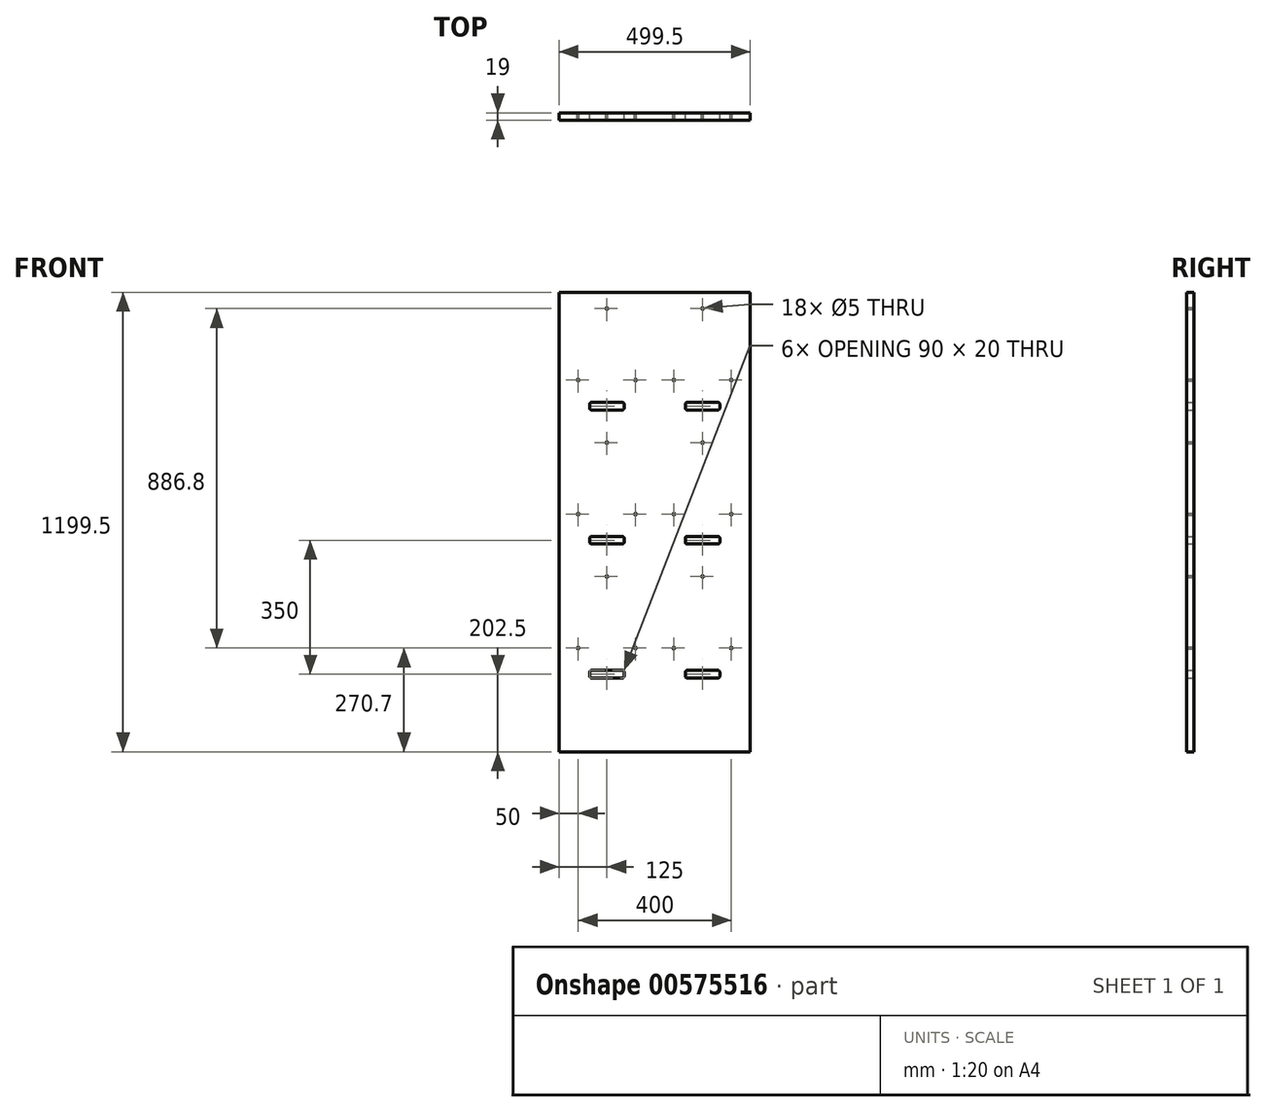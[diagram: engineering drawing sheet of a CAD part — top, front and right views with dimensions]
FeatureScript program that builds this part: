
annotation { "Feature Type Name" : "Feature", "Feature Type Description" : "" }
export const myFeature = defineFeature(function(context is Context, id is Id, definition is map)
    precondition{}
    {
        {
            var Q0;
            Q0=qCreatedBy(makeId("Front.planeOp"),FACE);
            var sketch = newSketch(context, id + "F0", { "sketchPlane" : qUnion([Q0])});
            skLineSegment(sketch, "E0.bottom", {"start": v(0, 0) * mm, "end": v(1000, 0) * mm, "construction": true});
            skLineSegment(sketch, "E0.left", {"start": v(0, 0) * mm, "end": v(0, 1590) * mm, "construction": true});
            skLineSegment(sketch, "E0.right", {"start": v(1000, 0) * mm, "end": v(1000, 1590) * mm, "construction": true});
            skLineSegment(sketch, "E1", {"start": v(500, 1590) * mm, "end": v(500, 0) * mm, "construction": true});
            skLineSegment(sketch, "E2.bottom", {"start": v(0, 1590) * mm, "end": v(1000, 1590) * mm, "construction": true});
            skLineSegment(sketch, "E2.left", {"start": v(0, 1590) * mm, "end": v(0, 290) * mm, "construction": true});
            skSolve(sketch);
        }
        {
            var Q0;
            Q0=qCreatedBy(makeId("Front.planeOp"),FACE);
            var sketch = newSketch(context, id + "F1", { "sketchPlane" : qUnion([Q0])});
            skLineSegment(sketch, "E3.bottom", {"start": v(0, 1590) * mm, "end": v(499.5, 1590) * mm});
            skLineSegment(sketch, "E3.top", {"start": v(0, 390.5) * mm, "end": v(499.5, 390.5) * mm});
            skLineSegment(sketch, "E3.left", {"start": v(0, 1590) * mm, "end": v(0, 390.5) * mm});
            skLineSegment(sketch, "E3.right", {"start": v(499.5, 1590) * mm, "end": v(499.5, 390.5) * mm});
            skLineSegment(sketch, "E4", {"start": v(125, 1590) * mm, "end": v(125, 390.5) * mm, "construction": true});
            skLineSegment(sketch, "E5", {"start": v(375, 1590) * mm, "end": v(375, 390.5) * mm, "construction": true});
            skCircle(sketch, "E6", {"center": v(125, 1548) * mm, "radius": 2.5 * mm});
            skCircle(sketch, "E7", {"center": v(50, 1361.2) * mm, "radius": 2.5 * mm});
            skCircle(sketch, "E8.MirrorC", {"center": v(200, 1361.2) * mm, "radius": 2.5 * mm});
            skLineSegment(sketch, "E9.bottom", {"start": v(165, 1283) * mm, "end": v(85, 1283) * mm});
            skLineSegment(sketch, "E9.top", {"start": v(165, 1303) * mm, "end": v(85, 1303) * mm});
            skLineSegment(sketch, "E9.left", {"start": v(170, 1288) * mm, "end": v(170, 1298) * mm});
            skLineSegment(sketch, "E9.right", {"start": v(80, 1288) * mm, "end": v(80, 1298) * mm});
            skPoint(sketch, "E9.middle", {"position": v(125, 1293) * mm});
            skPoint(sketch, "E10.visualSharp", {"position": v(80, 1303) * mm});
            skArc(sketch, "E10.filletArc", {"start": v(85, 1303) * mm, "mid": v(81.46, 1301.54) * mm, "end": v(80, 1298) * mm});
            skPoint(sketch, "E11.visualSharp", {"position": v(80, 1283) * mm});
            skArc(sketch, "E11.filletArc", {"start": v(80, 1288) * mm, "mid": v(81.46, 1284.46) * mm, "end": v(85, 1283) * mm});
            skPoint(sketch, "E12.visualSharp", {"position": v(170, 1283) * mm});
            skArc(sketch, "E12.filletArc", {"start": v(165, 1283) * mm, "mid": v(168.54, 1284.46) * mm, "end": v(170, 1288) * mm});
            skPoint(sketch, "E13.visualSharp", {"position": v(170, 1303) * mm});
            skArc(sketch, "E13.filletArc", {"start": v(170, 1298) * mm, "mid": v(168.54, 1301.54) * mm, "end": v(165, 1303) * mm});
            skLineSegment(sketch, "E14.0.1.0", {"start": v(165, 953) * mm, "end": v(85, 953) * mm});
            skPoint(sketch, "E14.0.1.1", {"position": v(125, 943) * mm});
            skPoint(sketch, "E14.0.1.2", {"position": v(80, 953) * mm});
            skPoint(sketch, "E14.0.1.3", {"position": v(80, 933) * mm});
            skPoint(sketch, "E14.0.1.4", {"position": v(170, 953) * mm});
            skLineSegment(sketch, "E14.0.1.5", {"start": v(165, 933) * mm, "end": v(85, 933) * mm});
            skPoint(sketch, "E14.0.1.6", {"position": v(170, 933) * mm});
            skCircle(sketch, "E14.0.1.7", {"center": v(125, 1198) * mm, "radius": 2.5 * mm});
            skCircle(sketch, "E14.0.1.8", {"center": v(200, 1011.2) * mm, "radius": 2.5 * mm});
            skCircle(sketch, "E14.0.1.9", {"center": v(50, 1011.2) * mm, "radius": 2.5 * mm});
            skArc(sketch, "E14.0.1.10", {"start": v(170, 948) * mm, "mid": v(168.54, 951.54) * mm, "end": v(165, 953) * mm});
            skArc(sketch, "E14.0.1.11", {"start": v(165, 933) * mm, "mid": v(168.54, 934.46) * mm, "end": v(170, 938) * mm});
            skArc(sketch, "E14.0.1.12", {"start": v(85, 953) * mm, "mid": v(81.46, 951.54) * mm, "end": v(80, 948) * mm});
            skLineSegment(sketch, "E14.0.1.13", {"start": v(170, 938) * mm, "end": v(170, 948) * mm});
            skLineSegment(sketch, "E14.0.1.14", {"start": v(80, 938) * mm, "end": v(80, 948) * mm});
            skArc(sketch, "E14.0.1.15", {"start": v(80, 938) * mm, "mid": v(81.46, 934.46) * mm, "end": v(85, 933) * mm});
            skLineSegment(sketch, "E14.0.2.0", {"start": v(165, 603) * mm, "end": v(85, 603) * mm});
            skPoint(sketch, "E14.0.2.1", {"position": v(125, 593) * mm});
            skPoint(sketch, "E14.0.2.2", {"position": v(80, 603) * mm});
            skPoint(sketch, "E14.0.2.3", {"position": v(80, 583) * mm});
            skPoint(sketch, "E14.0.2.4", {"position": v(170, 603) * mm});
            skLineSegment(sketch, "E14.0.2.5", {"start": v(165, 583) * mm, "end": v(85, 583) * mm});
            skPoint(sketch, "E14.0.2.6", {"position": v(170, 583) * mm});
            skCircle(sketch, "E14.0.2.7", {"center": v(125, 848) * mm, "radius": 2.5 * mm});
            skCircle(sketch, "E14.0.2.8", {"center": v(200, 661.2) * mm, "radius": 2.5 * mm});
            skCircle(sketch, "E14.0.2.9", {"center": v(50, 661.2) * mm, "radius": 2.5 * mm});
            skArc(sketch, "E14.0.2.10", {"start": v(170, 598) * mm, "mid": v(168.54, 601.54) * mm, "end": v(165, 603) * mm});
            skArc(sketch, "E14.0.2.11", {"start": v(165, 583) * mm, "mid": v(168.54, 584.46) * mm, "end": v(170, 588) * mm});
            skArc(sketch, "E14.0.2.12", {"start": v(85, 603) * mm, "mid": v(81.46, 601.54) * mm, "end": v(80, 598) * mm});
            skLineSegment(sketch, "E14.0.2.13", {"start": v(170, 588) * mm, "end": v(170, 598) * mm});
            skLineSegment(sketch, "E14.0.2.14", {"start": v(80, 588) * mm, "end": v(80, 598) * mm});
            skArc(sketch, "E14.0.2.15", {"start": v(80, 588) * mm, "mid": v(81.46, 584.46) * mm, "end": v(85, 583) * mm});
            skLineSegment(sketch, "E14.1.0.0", {"start": v(415, 1303) * mm, "end": v(335, 1303) * mm});
            skPoint(sketch, "E14.1.0.1", {"position": v(375, 1293) * mm});
            skPoint(sketch, "E14.1.0.2", {"position": v(330, 1303) * mm});
            skPoint(sketch, "E14.1.0.3", {"position": v(330, 1283) * mm});
            skPoint(sketch, "E14.1.0.4", {"position": v(420, 1303) * mm});
            skLineSegment(sketch, "E14.1.0.5", {"start": v(415, 1283) * mm, "end": v(335, 1283) * mm});
            skPoint(sketch, "E14.1.0.6", {"position": v(420, 1283) * mm});
            skCircle(sketch, "E14.1.0.7", {"center": v(375, 1548) * mm, "radius": 2.5 * mm});
            skCircle(sketch, "E14.1.0.8", {"center": v(450, 1361.2) * mm, "radius": 2.5 * mm});
            skCircle(sketch, "E14.1.0.9", {"center": v(300, 1361.2) * mm, "radius": 2.5 * mm});
            skArc(sketch, "E14.1.0.10", {"start": v(420, 1298) * mm, "mid": v(418.54, 1301.54) * mm, "end": v(415, 1303) * mm});
            skArc(sketch, "E14.1.0.11", {"start": v(415, 1283) * mm, "mid": v(418.54, 1284.46) * mm, "end": v(420, 1288) * mm});
            skArc(sketch, "E14.1.0.12", {"start": v(335, 1303) * mm, "mid": v(331.46, 1301.54) * mm, "end": v(330, 1298) * mm});
            skLineSegment(sketch, "E14.1.0.13", {"start": v(420, 1288) * mm, "end": v(420, 1298) * mm});
            skLineSegment(sketch, "E14.1.0.14", {"start": v(330, 1288) * mm, "end": v(330, 1298) * mm});
            skArc(sketch, "E14.1.0.15", {"start": v(330, 1288) * mm, "mid": v(331.46, 1284.46) * mm, "end": v(335, 1283) * mm});
            skLineSegment(sketch, "E14.1.1.0", {"start": v(415, 953) * mm, "end": v(335, 953) * mm});
            skPoint(sketch, "E14.1.1.1", {"position": v(375, 943) * mm});
            skPoint(sketch, "E14.1.1.2", {"position": v(330, 953) * mm});
            skPoint(sketch, "E14.1.1.3", {"position": v(330, 933) * mm});
            skPoint(sketch, "E14.1.1.4", {"position": v(420, 953) * mm});
            skLineSegment(sketch, "E14.1.1.5", {"start": v(415, 933) * mm, "end": v(335, 933) * mm});
            skPoint(sketch, "E14.1.1.6", {"position": v(420, 933) * mm});
            skCircle(sketch, "E14.1.1.7", {"center": v(375, 1198) * mm, "radius": 2.5 * mm});
            skCircle(sketch, "E14.1.1.8", {"center": v(450, 1011.2) * mm, "radius": 2.5 * mm});
            skCircle(sketch, "E14.1.1.9", {"center": v(300, 1011.2) * mm, "radius": 2.5 * mm});
            skArc(sketch, "E14.1.1.10", {"start": v(420, 948) * mm, "mid": v(418.54, 951.54) * mm, "end": v(415, 953) * mm});
            skArc(sketch, "E14.1.1.11", {"start": v(415, 933) * mm, "mid": v(418.54, 934.46) * mm, "end": v(420, 938) * mm});
            skArc(sketch, "E14.1.1.12", {"start": v(335, 953) * mm, "mid": v(331.46, 951.54) * mm, "end": v(330, 948) * mm});
            skLineSegment(sketch, "E14.1.1.13", {"start": v(420, 938) * mm, "end": v(420, 948) * mm});
            skLineSegment(sketch, "E14.1.1.14", {"start": v(330, 938) * mm, "end": v(330, 948) * mm});
            skArc(sketch, "E14.1.1.15", {"start": v(330, 938) * mm, "mid": v(331.46, 934.46) * mm, "end": v(335, 933) * mm});
            skLineSegment(sketch, "E14.1.2.0", {"start": v(415, 603) * mm, "end": v(335, 603) * mm});
            skPoint(sketch, "E14.1.2.1", {"position": v(375, 593) * mm});
            skPoint(sketch, "E14.1.2.2", {"position": v(330, 603) * mm});
            skPoint(sketch, "E14.1.2.3", {"position": v(330, 583) * mm});
            skPoint(sketch, "E14.1.2.4", {"position": v(420, 603) * mm});
            skLineSegment(sketch, "E14.1.2.5", {"start": v(415, 583) * mm, "end": v(335, 583) * mm});
            skPoint(sketch, "E14.1.2.6", {"position": v(420, 583) * mm});
            skCircle(sketch, "E14.1.2.7", {"center": v(375, 848) * mm, "radius": 2.5 * mm});
            skCircle(sketch, "E14.1.2.8", {"center": v(450, 661.2) * mm, "radius": 2.5 * mm});
            skCircle(sketch, "E14.1.2.9", {"center": v(300, 661.2) * mm, "radius": 2.5 * mm});
            skArc(sketch, "E14.1.2.10", {"start": v(420, 598) * mm, "mid": v(418.54, 601.54) * mm, "end": v(415, 603) * mm});
            skArc(sketch, "E14.1.2.11", {"start": v(415, 583) * mm, "mid": v(418.54, 584.46) * mm, "end": v(420, 588) * mm});
            skArc(sketch, "E14.1.2.12", {"start": v(335, 603) * mm, "mid": v(331.46, 601.54) * mm, "end": v(330, 598) * mm});
            skLineSegment(sketch, "E14.1.2.13", {"start": v(420, 588) * mm, "end": v(420, 598) * mm});
            skLineSegment(sketch, "E14.1.2.14", {"start": v(330, 588) * mm, "end": v(330, 598) * mm});
            skArc(sketch, "E14.1.2.15", {"start": v(330, 588) * mm, "mid": v(331.46, 584.46) * mm, "end": v(335, 583) * mm});
            skLineSegment(sketch, "E14.direction1", {"start": v(80, 1283) * mm, "end": v(330, 1283) * mm, "construction": true});
            skLineSegment(sketch, "E14.direction2", {"start": v(80, 1283) * mm, "end": v(80, 933) * mm, "construction": true});
            skLineSegment(sketch, "E15.MirrorCS", {"start": v(580, 938) * mm, "end": v(580, 948) * mm});
            skLineSegment(sketch, "E16.MirrorCS", {"start": v(580, 1288) * mm, "end": v(580, 1298) * mm});
            skArc(sketch, "E17.MirrorCS", {"start": v(585, 583) * mm, "mid": v(581.46, 584.46) * mm, "end": v(580, 588) * mm});
            skLineSegment(sketch, "E18.MirrorCS", {"start": v(835, 1283) * mm, "end": v(915, 1283) * mm});
            skArc(sketch, "E19.MirrorCS", {"start": v(830, 598) * mm, "mid": v(831.46, 601.54) * mm, "end": v(835, 603) * mm});
            skLineSegment(sketch, "E20.MirrorCS", {"start": v(830, 588) * mm, "end": v(830, 598) * mm});
            skArc(sketch, "E21.MirrorCS", {"start": v(830, 948) * mm, "mid": v(831.46, 951.54) * mm, "end": v(835, 953) * mm});
            skArc(sketch, "E22.MirrorCS", {"start": v(830, 1298) * mm, "mid": v(831.46, 1301.54) * mm, "end": v(835, 1303) * mm});
            skLineSegment(sketch, "E23.MirrorCS", {"start": v(830, 938) * mm, "end": v(830, 948) * mm});
            skArc(sketch, "E24.MirrorCS", {"start": v(580, 948) * mm, "mid": v(581.46, 951.54) * mm, "end": v(585, 953) * mm});
            skArc(sketch, "E25.MirrorCS", {"start": v(915, 1303) * mm, "mid": v(918.54, 1301.54) * mm, "end": v(920, 1298) * mm});
            skArc(sketch, "E26.MirrorCS", {"start": v(580, 1298) * mm, "mid": v(581.46, 1301.54) * mm, "end": v(585, 1303) * mm});
            skArc(sketch, "E27.MirrorCS", {"start": v(580, 598) * mm, "mid": v(581.46, 601.54) * mm, "end": v(585, 603) * mm});
            skArc(sketch, "E28.MirrorCS", {"start": v(835, 1283) * mm, "mid": v(831.46, 1284.46) * mm, "end": v(830, 1288) * mm});
            skLineSegment(sketch, "E29.MirrorCS", {"start": v(835, 1303) * mm, "end": v(915, 1303) * mm});
            skArc(sketch, "E30.MirrorCS", {"start": v(835, 583) * mm, "mid": v(831.46, 584.46) * mm, "end": v(830, 588) * mm});
            skLineSegment(sketch, "E31.MirrorCS", {"start": v(830, 1288) * mm, "end": v(830, 1298) * mm});
            skLineSegment(sketch, "E32.MirrorCS", {"start": v(580, 588) * mm, "end": v(580, 598) * mm});
            skArc(sketch, "E33.MirrorCS", {"start": v(835, 933) * mm, "mid": v(831.46, 934.46) * mm, "end": v(830, 938) * mm});
            skLineSegment(sketch, "E34.MirrorCS", {"start": v(920, 1288) * mm, "end": v(920, 1298) * mm});
            skArc(sketch, "E35.MirrorCS", {"start": v(920, 1288) * mm, "mid": v(918.54, 1284.46) * mm, "end": v(915, 1283) * mm});
            skArc(sketch, "E36.MirrorCS", {"start": v(585, 933) * mm, "mid": v(581.46, 934.46) * mm, "end": v(580, 938) * mm});
            skArc(sketch, "E37.MirrorCS", {"start": v(585, 1283) * mm, "mid": v(581.46, 1284.46) * mm, "end": v(580, 1288) * mm});
            skLineSegment(sketch, "E38.MirrorCS", {"start": v(585, 1283) * mm, "end": v(665, 1283) * mm});
            skArc(sketch, "E39.MirrorCS", {"start": v(670, 1288) * mm, "mid": v(668.54, 1284.46) * mm, "end": v(665, 1283) * mm});
            skLineSegment(sketch, "E40.MirrorCS", {"start": v(670, 1288) * mm, "end": v(670, 1298) * mm});
            skArc(sketch, "E41.MirrorCS", {"start": v(665, 953) * mm, "mid": v(668.54, 951.54) * mm, "end": v(670, 948) * mm});
            skArc(sketch, "E42.MirrorCS", {"start": v(665, 1303) * mm, "mid": v(668.54, 1301.54) * mm, "end": v(670, 1298) * mm});
            skArc(sketch, "E43.MirrorCS", {"start": v(915, 603) * mm, "mid": v(918.54, 601.54) * mm, "end": v(920, 598) * mm});
            skLineSegment(sketch, "E44.MirrorCS", {"start": v(585, 1303) * mm, "end": v(665, 1303) * mm});
            skLineSegment(sketch, "E45.MirrorCS", {"start": v(920, 938) * mm, "end": v(920, 948) * mm});
            skLineSegment(sketch, "E46.MirrorCS", {"start": v(585, 953) * mm, "end": v(665, 953) * mm});
            skArc(sketch, "E47.MirrorCS", {"start": v(920, 588) * mm, "mid": v(918.54, 584.46) * mm, "end": v(915, 583) * mm});
            skArc(sketch, "E48.MirrorCS", {"start": v(920, 938) * mm, "mid": v(918.54, 934.46) * mm, "end": v(915, 933) * mm});
            skLineSegment(sketch, "E49.MirrorCS", {"start": v(835, 583) * mm, "end": v(915, 583) * mm});
            skArc(sketch, "E50.MirrorCS", {"start": v(915, 953) * mm, "mid": v(918.54, 951.54) * mm, "end": v(920, 948) * mm});
            skLineSegment(sketch, "E51.MirrorCS", {"start": v(670, 588) * mm, "end": v(670, 598) * mm});
            skLineSegment(sketch, "E52.MirrorCS", {"start": v(670, 938) * mm, "end": v(670, 948) * mm});
            skArc(sketch, "E53.MirrorCS", {"start": v(670, 588) * mm, "mid": v(668.54, 584.46) * mm, "end": v(665, 583) * mm});
            skLineSegment(sketch, "E54.MirrorCS", {"start": v(585, 603) * mm, "end": v(665, 603) * mm});
            skLineSegment(sketch, "E55.MirrorCS", {"start": v(835, 933) * mm, "end": v(915, 933) * mm});
            skLineSegment(sketch, "E56.MirrorCS", {"start": v(585, 583) * mm, "end": v(665, 583) * mm});
            skArc(sketch, "E57.MirrorCS", {"start": v(665, 603) * mm, "mid": v(668.54, 601.54) * mm, "end": v(670, 598) * mm});
            skArc(sketch, "E58.MirrorCS", {"start": v(670, 938) * mm, "mid": v(668.54, 934.46) * mm, "end": v(665, 933) * mm});
            skLineSegment(sketch, "E59.MirrorCS", {"start": v(835, 953) * mm, "end": v(915, 953) * mm});
            skLineSegment(sketch, "E60.MirrorCS", {"start": v(920, 588) * mm, "end": v(920, 598) * mm});
            skLineSegment(sketch, "E61.MirrorCS", {"start": v(585, 933) * mm, "end": v(665, 933) * mm});
            skLineSegment(sketch, "E62.MirrorCS", {"start": v(835, 603) * mm, "end": v(915, 603) * mm});
            skCircle(sketch, "E63.MirrorC", {"center": v(800, 661.2) * mm, "radius": 2.5 * mm});
            skCircle(sketch, "E64.MirrorC", {"center": v(950, 1011.2) * mm, "radius": 2.5 * mm});
            skCircle(sketch, "E65.MirrorC", {"center": v(550, 1361.2) * mm, "radius": 2.5 * mm});
            skCircle(sketch, "E66.MirrorC", {"center": v(875, 1548) * mm, "radius": 2.5 * mm});
            skCircle(sketch, "E67.MirrorC", {"center": v(875, 1198) * mm, "radius": 2.5 * mm});
            skCircle(sketch, "E68.MirrorC", {"center": v(875, 848) * mm, "radius": 2.5 * mm});
            skCircle(sketch, "E69.MirrorC", {"center": v(950, 661.2) * mm, "radius": 2.5 * mm});
            skCircle(sketch, "E70.MirrorC", {"center": v(550, 1011.2) * mm, "radius": 2.5 * mm});
            skCircle(sketch, "E71.MirrorC", {"center": v(625, 848) * mm, "radius": 2.5 * mm});
            skCircle(sketch, "E72.MirrorC", {"center": v(700, 1011.2) * mm, "radius": 2.5 * mm});
            skCircle(sketch, "E73.MirrorC", {"center": v(700, 661.2) * mm, "radius": 2.5 * mm});
            skCircle(sketch, "E74.MirrorC", {"center": v(625, 1548) * mm, "radius": 2.5 * mm});
            skCircle(sketch, "E75.MirrorC", {"center": v(800, 1361.2) * mm, "radius": 2.5 * mm});
            skCircle(sketch, "E76.MirrorC", {"center": v(800, 1011.2) * mm, "radius": 2.5 * mm});
            skPoint(sketch, "E77.MirrorP", {"position": v(875, 1293) * mm});
            skCircle(sketch, "E78.MirrorC", {"center": v(700, 1361.2) * mm, "radius": 2.5 * mm});
            skPoint(sketch, "E79.MirrorP", {"position": v(625, 1293) * mm});
            skCircle(sketch, "E80.MirrorC", {"center": v(950, 1361.2) * mm, "radius": 2.5 * mm});
            skPoint(sketch, "E81.MirrorP", {"position": v(920, 1303) * mm});
            skCircle(sketch, "E82.MirrorC", {"center": v(550, 661.2) * mm, "radius": 2.5 * mm});
            skCircle(sketch, "E83.MirrorC", {"center": v(625, 1198) * mm, "radius": 2.5 * mm});
            skLineSegment(sketch, "E84.MirrorCS", {"start": v(920, 1283) * mm, "end": v(920, 933) * mm, "construction": true});
            skPoint(sketch, "E85.MirrorP", {"position": v(580, 603) * mm});
            skPoint(sketch, "E86.MirrorP", {"position": v(625, 943) * mm});
            skPoint(sketch, "E87.MirrorP", {"position": v(580, 953) * mm});
            skPoint(sketch, "E88.MirrorP", {"position": v(670, 953) * mm});
            skPoint(sketch, "E89.MirrorP", {"position": v(830, 603) * mm});
            skPoint(sketch, "E90.MirrorP", {"position": v(580, 1303) * mm});
            skPoint(sketch, "E91.MirrorP", {"position": v(920, 953) * mm});
            skPoint(sketch, "E92.MirrorP", {"position": v(830, 583) * mm});
            skPoint(sketch, "E93.MirrorP", {"position": v(920, 933) * mm});
            skPoint(sketch, "E94.MirrorP", {"position": v(830, 1283) * mm});
            skPoint(sketch, "E95.MirrorP", {"position": v(670, 1303) * mm});
            skPoint(sketch, "E96.MirrorP", {"position": v(580, 1283) * mm});
            skPoint(sketch, "E97.MirrorP", {"position": v(670, 583) * mm});
            skPoint(sketch, "E98.MirrorP", {"position": v(830, 1303) * mm});
            skLineSegment(sketch, "E99.MirrorCS", {"start": v(625, 1590) * mm, "end": v(625, 390.5) * mm, "construction": true});
            skLineSegment(sketch, "E100.MirrorCS", {"start": v(875, 1590) * mm, "end": v(875, 390.5) * mm, "construction": true});
            skLineSegment(sketch, "E101.MirrorCS", {"start": v(920, 1283) * mm, "end": v(670, 1283) * mm, "construction": true});
            skPoint(sketch, "E102.MirrorP", {"position": v(830, 953) * mm});
            skPoint(sketch, "E103.MirrorP", {"position": v(830, 933) * mm});
            skPoint(sketch, "E104.MirrorP", {"position": v(580, 583) * mm});
            skPoint(sketch, "E105.MirrorP", {"position": v(875, 943) * mm});
            skPoint(sketch, "E106.MirrorP", {"position": v(670, 1283) * mm});
            skPoint(sketch, "E107.MirrorP", {"position": v(580, 933) * mm});
            skLineSegment(sketch, "E108.MirrorCS", {"start": v(1000, 1590) * mm, "end": v(1000, 390.5) * mm});
            skPoint(sketch, "E109.MirrorP", {"position": v(625, 593) * mm});
            skLineSegment(sketch, "E110.MirrorCS", {"start": v(1000, 390.5) * mm, "end": v(500.5, 390.5) * mm});
            skPoint(sketch, "E111.MirrorP", {"position": v(875, 593) * mm});
            skPoint(sketch, "E112.MirrorP", {"position": v(920, 583) * mm});
            skLineSegment(sketch, "E113.MirrorCS", {"start": v(1000, 1590) * mm, "end": v(500.5, 1590) * mm});
            skPoint(sketch, "E114.MirrorP", {"position": v(920, 603) * mm});
            skPoint(sketch, "E115.MirrorP", {"position": v(670, 603) * mm});
            skPoint(sketch, "E116.MirrorP", {"position": v(670, 933) * mm});
            skPoint(sketch, "E117.MirrorP", {"position": v(920, 1283) * mm});
            skLineSegment(sketch, "E118.MirrorCS", {"start": v(500.5, 1590) * mm, "end": v(500.5, 390.5) * mm});
            skSolve(sketch);
        }
        {
            var Q0;
            Q0=makeQuery(id+"F1.imprint","IMPRINT",FACE,{"disambiguationData":[TD([[makeQuery(id+"F1.imprint","IMPRINT",EDGE,{"derivedFrom":sQuery(id+"F1.wireOp",EDGE,"E3.bottom")}),-1.0]])]});
            extrude(context, id + "F2", {"entities" : qUnion([Q0]), "depth" : 19 * mm, "offsetDistance" : 25 * mm});
        }
        {
            var Q0;
            Q0=makeQuery(id+"F2.opExtrude","SWEPT_BODY",BODY,{"disambiguationData":[OSD([sQuery(id+"F1.wireOp",EDGE,"E3.bottom"),sQuery(id+"F1.wireOp",EDGE,"E3.top"),sQuery(id+"F1.wireOp",EDGE,"E3.left"),sQuery(id+"F1.wireOp",EDGE,"E3.right"),sQuery(id+"F1.wireOp",EDGE,"E6"),sQuery(id+"F1.wireOp",EDGE,"E7"),sQuery(id+"F1.wireOp",EDGE,"E8.MirrorC"),sQuery(id+"F1.wireOp",EDGE,"E9.bottom"),sQuery(id+"F1.wireOp",EDGE,"E9.top"),sQuery(id+"F1.wireOp",EDGE,"E9.left"),sQuery(id+"F1.wireOp",EDGE,"E9.right"),sQuery(id+"F1.wireOp",EDGE,"E10.filletArc"),sQuery(id+"F1.wireOp",EDGE,"E11.filletArc"),sQuery(id+"F1.wireOp",EDGE,"E12.filletArc"),sQuery(id+"F1.wireOp",EDGE,"E13.filletArc"),sQuery(id+"F1.wireOp",EDGE,"E14.0.1.0"),sQuery(id+"F1.wireOp",EDGE,"E14.0.1.5"),sQuery(id+"F1.wireOp",EDGE,"E14.0.1.7"),sQuery(id+"F1.wireOp",EDGE,"E14.0.1.8"),sQuery(id+"F1.wireOp",EDGE,"E14.0.1.9"),sQuery(id+"F1.wireOp",EDGE,"E14.0.1.10"),sQuery(id+"F1.wireOp",EDGE,"E14.0.1.11"),sQuery(id+"F1.wireOp",EDGE,"E14.0.1.12"),sQuery(id+"F1.wireOp",EDGE,"E14.0.1.13"),sQuery(id+"F1.wireOp",EDGE,"E14.0.1.14"),sQuery(id+"F1.wireOp",EDGE,"E14.0.1.15"),sQuery(id+"F1.wireOp",EDGE,"E14.0.2.0"),sQuery(id+"F1.wireOp",EDGE,"E14.0.2.5"),sQuery(id+"F1.wireOp",EDGE,"E14.0.2.7"),sQuery(id+"F1.wireOp",EDGE,"E14.0.2.8"),sQuery(id+"F1.wireOp",EDGE,"E14.0.2.9"),sQuery(id+"F1.wireOp",EDGE,"E14.0.2.10"),sQuery(id+"F1.wireOp",EDGE,"E14.0.2.11"),sQuery(id+"F1.wireOp",EDGE,"E14.0.2.12"),sQuery(id+"F1.wireOp",EDGE,"E14.0.2.13"),sQuery(id+"F1.wireOp",EDGE,"E14.0.2.14"),sQuery(id+"F1.wireOp",EDGE,"E14.0.2.15"),sQuery(id+"F1.wireOp",EDGE,"E14.1.0.0"),sQuery(id+"F1.wireOp",EDGE,"E14.1.0.5"),sQuery(id+"F1.wireOp",EDGE,"E14.1.0.7"),sQuery(id+"F1.wireOp",EDGE,"E14.1.0.8"),sQuery(id+"F1.wireOp",EDGE,"E14.1.0.9"),sQuery(id+"F1.wireOp",EDGE,"E14.1.0.10"),sQuery(id+"F1.wireOp",EDGE,"E14.1.0.11"),sQuery(id+"F1.wireOp",EDGE,"E14.1.0.12"),sQuery(id+"F1.wireOp",EDGE,"E14.1.0.13"),sQuery(id+"F1.wireOp",EDGE,"E14.1.0.14"),sQuery(id+"F1.wireOp",EDGE,"E14.1.0.15"),sQuery(id+"F1.wireOp",EDGE,"E14.1.1.0"),sQuery(id+"F1.wireOp",EDGE,"E14.1.1.5"),sQuery(id+"F1.wireOp",EDGE,"E14.1.1.7"),sQuery(id+"F1.wireOp",EDGE,"E14.1.1.8"),sQuery(id+"F1.wireOp",EDGE,"E14.1.1.9"),sQuery(id+"F1.wireOp",EDGE,"E14.1.1.10"),sQuery(id+"F1.wireOp",EDGE,"E14.1.1.11"),sQuery(id+"F1.wireOp",EDGE,"E14.1.1.12"),sQuery(id+"F1.wireOp",EDGE,"E14.1.1.13"),sQuery(id+"F1.wireOp",EDGE,"E14.1.1.14"),sQuery(id+"F1.wireOp",EDGE,"E14.1.1.15"),sQuery(id+"F1.wireOp",EDGE,"E14.1.2.0"),sQuery(id+"F1.wireOp",EDGE,"E14.1.2.5"),sQuery(id+"F1.wireOp",EDGE,"E14.1.2.7"),sQuery(id+"F1.wireOp",EDGE,"E14.1.2.8"),sQuery(id+"F1.wireOp",EDGE,"E14.1.2.9"),sQuery(id+"F1.wireOp",EDGE,"E14.1.2.10"),sQuery(id+"F1.wireOp",EDGE,"E14.1.2.11"),sQuery(id+"F1.wireOp",EDGE,"E14.1.2.12"),sQuery(id+"F1.wireOp",EDGE,"E14.1.2.13"),sQuery(id+"F1.wireOp",EDGE,"E14.1.2.14"),sQuery(id+"F1.wireOp",EDGE,"E14.1.2.15")])]});
            var Q1;
            Q1=sQuery(id+"F1.wireOp",VERTEX,"E3.top.start");
            var Q2;
            Q2=sQuery(id+"F0.wireOp",VERTEX,"E0.bottom.start");
            transform(context, id + "F3", {"entities" : qUnion([Q0]), "transformType" : TransformType.TRANSLATION_ENTITY, "oppositeDirectionEntity" : false, "transformLine" : qUnion([Q1, Q2]), "makeCopy" : false});
        }
    });
